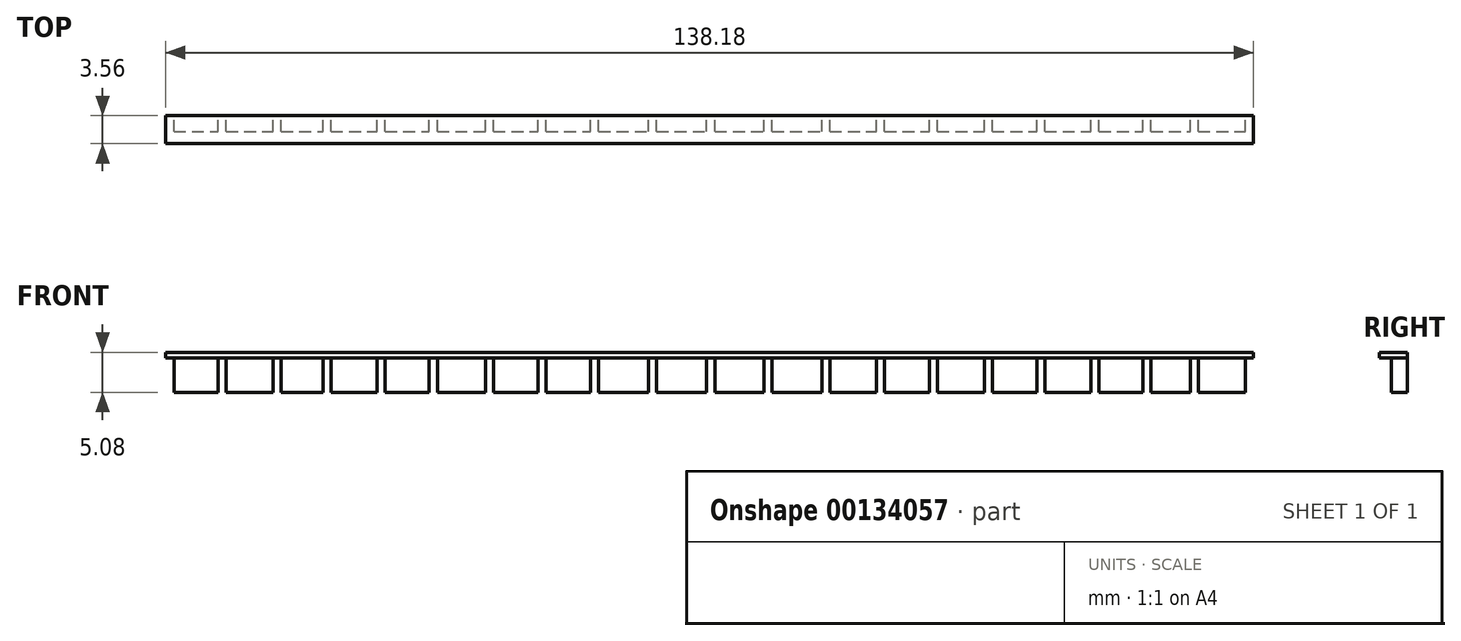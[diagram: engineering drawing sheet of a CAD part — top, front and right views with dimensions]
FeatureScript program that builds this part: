
annotation { "Feature Type Name" : "Feature", "Feature Type Description" : "" }
export const myFeature = defineFeature(function(context is Context, id is Id, definition is map)
    precondition{}
    {
        {
            var Q0;
            Q0=qCreatedBy(makeId("Front.planeOp"),FACE);
            var sketch = newSketch(context, id + "F0", { "sketchPlane" : qUnion([Q0])});
            skLineSegment(sketch, "E0.bottom", {"start": v(69.09, 2.54) * mm, "end": v(-69.09, 2.54) * mm});
            skLineSegment(sketch, "E0.top", {"start": v(69.09, -2.54) * mm, "end": v(-69.09, -2.54) * mm});
            skLineSegment(sketch, "E0.left", {"start": v(69.09, 2.54) * mm, "end": v(69.09, -2.54) * mm});
            skLineSegment(sketch, "E0.right", {"start": v(-69.09, 2.54) * mm, "end": v(-69.09, -2.54) * mm});
            skPoint(sketch, "E0.middle", {"position": v(0, 0) * mm});
            skLineSegment(sketch, "E1", {"start": v(-69.09, 1.8) * mm, "end": v(69.09, 1.8) * mm});
            skLineSegment(sketch, "E2.bottom", {"start": v(69.09, -2.54) * mm, "end": v(68.05, -2.54) * mm});
            skLineSegment(sketch, "E2.top", {"start": v(69.09, 1.8) * mm, "end": v(68.05, 1.8) * mm});
            skLineSegment(sketch, "E2.left", {"start": v(69.09, -2.54) * mm, "end": v(69.09, 1.8) * mm});
            skLineSegment(sketch, "E2.right", {"start": v(68.05, -2.54) * mm, "end": v(68.05, 1.8) * mm});
            skLineSegment(sketch, "E3.bottom", {"start": v(62.09, -2.54) * mm, "end": v(61.12, -2.54) * mm});
            skLineSegment(sketch, "E3.top", {"start": v(62.09, 1.8) * mm, "end": v(61.12, 1.8) * mm});
            skLineSegment(sketch, "E3.left", {"start": v(62.09, -2.54) * mm, "end": v(62.09, 1.8) * mm});
            skLineSegment(sketch, "E3.right", {"start": v(61.12, -2.54) * mm, "end": v(61.12, 1.8) * mm});
            skLineSegment(sketch, "E4.bottom", {"start": v(56.07, -2.54) * mm, "end": v(55.05, -2.54) * mm});
            skLineSegment(sketch, "E4.top", {"start": v(56.07, 1.8) * mm, "end": v(55.05, 1.8) * mm});
            skLineSegment(sketch, "E4.left", {"start": v(56.07, -2.54) * mm, "end": v(56.07, 1.8) * mm});
            skLineSegment(sketch, "E4.right", {"start": v(55.05, -2.54) * mm, "end": v(55.05, 1.8) * mm});
            skLineSegment(sketch, "E5.bottom", {"start": v(49.46, -2.54) * mm, "end": v(48.44, -2.54) * mm});
            skLineSegment(sketch, "E5.top", {"start": v(49.46, 1.8) * mm, "end": v(48.44, 1.8) * mm});
            skLineSegment(sketch, "E5.left", {"start": v(49.46, -2.54) * mm, "end": v(49.46, 1.8) * mm});
            skLineSegment(sketch, "E5.right", {"start": v(48.44, -2.54) * mm, "end": v(48.44, 1.8) * mm});
            skLineSegment(sketch, "E6.bottom", {"start": v(42.59, -2.54) * mm, "end": v(41.57, -2.54) * mm});
            skLineSegment(sketch, "E6.top", {"start": v(42.59, 1.8) * mm, "end": v(41.57, 1.8) * mm});
            skLineSegment(sketch, "E6.left", {"start": v(42.59, -2.54) * mm, "end": v(42.59, 1.8) * mm});
            skLineSegment(sketch, "E6.right", {"start": v(41.57, -2.54) * mm, "end": v(41.57, 1.8) * mm});
            skLineSegment(sketch, "E7.bottom", {"start": v(35.92, -2.54) * mm, "end": v(34.9, -2.54) * mm});
            skLineSegment(sketch, "E7.top", {"start": v(35.92, 1.8) * mm, "end": v(34.9, 1.8) * mm});
            skLineSegment(sketch, "E7.left", {"start": v(35.92, -2.54) * mm, "end": v(35.92, 1.8) * mm});
            skLineSegment(sketch, "E7.right", {"start": v(34.9, -2.54) * mm, "end": v(34.9, 1.8) * mm});
            skLineSegment(sketch, "E8.bottom", {"start": v(28.94, -2.54) * mm, "end": v(27.92, -2.54) * mm});
            skLineSegment(sketch, "E8.top", {"start": v(28.94, 1.8) * mm, "end": v(27.92, 1.8) * mm});
            skLineSegment(sketch, "E8.left", {"start": v(28.94, -2.54) * mm, "end": v(28.94, 1.8) * mm});
            skLineSegment(sketch, "E8.right", {"start": v(27.92, -2.54) * mm, "end": v(27.92, 1.8) * mm});
            skLineSegment(sketch, "E9.bottom", {"start": v(22.23, -2.54) * mm, "end": v(21.2, -2.54) * mm});
            skLineSegment(sketch, "E9.top", {"start": v(22.23, 1.8) * mm, "end": v(21.2, 1.8) * mm});
            skLineSegment(sketch, "E9.left", {"start": v(22.23, -2.54) * mm, "end": v(22.23, 1.8) * mm});
            skLineSegment(sketch, "E9.right", {"start": v(21.2, -2.54) * mm, "end": v(21.2, 1.8) * mm});
            skLineSegment(sketch, "E10.bottom", {"start": v(15.3, -2.54) * mm, "end": v(14.27, -2.54) * mm});
            skLineSegment(sketch, "E10.top", {"start": v(15.3, 1.8) * mm, "end": v(14.27, 1.8) * mm});
            skLineSegment(sketch, "E10.left", {"start": v(15.3, -2.54) * mm, "end": v(15.3, 1.8) * mm});
            skLineSegment(sketch, "E10.right", {"start": v(14.27, -2.54) * mm, "end": v(14.27, 1.8) * mm});
            skLineSegment(sketch, "E11.bottom", {"start": v(7.94, -2.54) * mm, "end": v(6.91, -2.54) * mm});
            skLineSegment(sketch, "E11.top", {"start": v(7.94, 1.8) * mm, "end": v(6.91, 1.8) * mm});
            skLineSegment(sketch, "E11.left", {"start": v(7.94, -2.54) * mm, "end": v(7.94, 1.8) * mm});
            skLineSegment(sketch, "E11.right", {"start": v(6.91, -2.54) * mm, "end": v(6.91, 1.8) * mm});
            skLineSegment(sketch, "E12.bottom", {"start": v(0.68, -2.54) * mm, "end": v(-0.37, -2.54) * mm});
            skLineSegment(sketch, "E12.top", {"start": v(0.68, 1.8) * mm, "end": v(-0.37, 1.8) * mm});
            skLineSegment(sketch, "E12.left", {"start": v(0.68, -2.54) * mm, "end": v(0.68, 1.8) * mm});
            skLineSegment(sketch, "E12.right", {"start": v(-0.37, -2.54) * mm, "end": v(-0.37, 1.8) * mm});
            skLineSegment(sketch, "E13.bottom", {"start": v(-6.72, -2.54) * mm, "end": v(-7.73, -2.54) * mm});
            skLineSegment(sketch, "E13.top", {"start": v(-6.72, 1.8) * mm, "end": v(-7.73, 1.8) * mm});
            skLineSegment(sketch, "E13.left", {"start": v(-6.72, -2.54) * mm, "end": v(-6.72, 1.8) * mm});
            skLineSegment(sketch, "E13.right", {"start": v(-7.73, -2.54) * mm, "end": v(-7.73, 1.8) * mm});
            skLineSegment(sketch, "E14.bottom", {"start": v(-14.09, -2.54) * mm, "end": v(-15.13, -2.54) * mm});
            skLineSegment(sketch, "E14.top", {"start": v(-14.09, 1.8) * mm, "end": v(-15.13, 1.8) * mm});
            skLineSegment(sketch, "E14.left", {"start": v(-14.09, -2.54) * mm, "end": v(-14.09, 1.8) * mm});
            skLineSegment(sketch, "E14.right", {"start": v(-15.13, -2.54) * mm, "end": v(-15.13, 1.8) * mm});
            skLineSegment(sketch, "E15.bottom", {"start": v(-20.76, -2.54) * mm, "end": v(-21.8, -2.54) * mm});
            skLineSegment(sketch, "E15.top", {"start": v(-20.76, 1.8) * mm, "end": v(-21.8, 1.8) * mm});
            skLineSegment(sketch, "E15.left", {"start": v(-20.76, -2.54) * mm, "end": v(-20.76, 1.8) * mm});
            skLineSegment(sketch, "E15.right", {"start": v(-21.8, -2.54) * mm, "end": v(-21.8, 1.8) * mm});
            skLineSegment(sketch, "E16.bottom", {"start": v(-27.44, -2.54) * mm, "end": v(-28.46, -2.54) * mm});
            skLineSegment(sketch, "E16.top", {"start": v(-27.44, 1.8) * mm, "end": v(-28.46, 1.8) * mm});
            skLineSegment(sketch, "E16.left", {"start": v(-27.44, -2.54) * mm, "end": v(-27.44, 1.8) * mm});
            skLineSegment(sketch, "E16.right", {"start": v(-28.46, -2.54) * mm, "end": v(-28.46, 1.8) * mm});
            skLineSegment(sketch, "E17.bottom", {"start": v(-34.57, -2.54) * mm, "end": v(-35.6, -2.54) * mm});
            skLineSegment(sketch, "E17.top", {"start": v(-34.57, 1.8) * mm, "end": v(-35.6, 1.8) * mm});
            skLineSegment(sketch, "E17.left", {"start": v(-34.57, -2.54) * mm, "end": v(-34.57, 1.8) * mm});
            skLineSegment(sketch, "E17.right", {"start": v(-35.6, -2.54) * mm, "end": v(-35.6, 1.8) * mm});
            skLineSegment(sketch, "E18.bottom", {"start": v(-41.2, -2.54) * mm, "end": v(-42.23, -2.54) * mm});
            skLineSegment(sketch, "E18.top", {"start": v(-41.2, 1.8) * mm, "end": v(-42.23, 1.8) * mm});
            skLineSegment(sketch, "E18.left", {"start": v(-41.2, -2.54) * mm, "end": v(-41.2, 1.8) * mm});
            skLineSegment(sketch, "E18.right", {"start": v(-42.23, -2.54) * mm, "end": v(-42.23, 1.8) * mm});
            skLineSegment(sketch, "E19.bottom", {"start": v(-48.08, -2.54) * mm, "end": v(-49.1, -2.54) * mm});
            skLineSegment(sketch, "E19.top", {"start": v(-48.08, 1.8) * mm, "end": v(-49.1, 1.8) * mm});
            skLineSegment(sketch, "E19.left", {"start": v(-48.08, -2.54) * mm, "end": v(-48.08, 1.8) * mm});
            skLineSegment(sketch, "E19.right", {"start": v(-49.1, -2.54) * mm, "end": v(-49.1, 1.8) * mm});
            skLineSegment(sketch, "E20.bottom", {"start": v(-54.41, -2.54) * mm, "end": v(-55.44, -2.54) * mm});
            skLineSegment(sketch, "E20.top", {"start": v(-54.41, 1.8) * mm, "end": v(-55.44, 1.8) * mm});
            skLineSegment(sketch, "E20.left", {"start": v(-54.41, -2.54) * mm, "end": v(-54.41, 1.8) * mm});
            skLineSegment(sketch, "E20.right", {"start": v(-55.44, -2.54) * mm, "end": v(-55.44, 1.8) * mm});
            skLineSegment(sketch, "E21.bottom", {"start": v(-61.4, -2.54) * mm, "end": v(-62.43, -2.54) * mm});
            skLineSegment(sketch, "E21.top", {"start": v(-61.4, 1.8) * mm, "end": v(-62.43, 1.8) * mm});
            skLineSegment(sketch, "E21.left", {"start": v(-61.4, -2.54) * mm, "end": v(-61.4, 1.8) * mm});
            skLineSegment(sketch, "E21.right", {"start": v(-62.43, -2.54) * mm, "end": v(-62.43, 1.8) * mm});
            skLineSegment(sketch, "E22.bottom", {"start": v(-69.09, -2.54) * mm, "end": v(-68.04, -2.54) * mm});
            skLineSegment(sketch, "E22.top", {"start": v(-69.09, 1.8) * mm, "end": v(-68.04, 1.8) * mm});
            skLineSegment(sketch, "E22.left", {"start": v(-69.09, -2.54) * mm, "end": v(-69.09, 1.8) * mm});
            skLineSegment(sketch, "E22.right", {"start": v(-68.04, -2.54) * mm, "end": v(-68.04, 1.8) * mm});
            skSolve(sketch);
        }
        {
            var Q0;
            Q0=makeQuery(id+"F0.imprint","IMPRINT",FACE,{"disambiguationData":[TD([[makeQuery(id+"F0.imprint","IMPRINT",EDGE,{"derivedFrom":sQuery(id+"F0.wireOp",EDGE,"E22.bottom")}),1.0]])]});
            var Q1;
            Q1=makeQuery(id+"F0.imprint","IMPRINT",FACE,{"disambiguationData":[TD([[makeQuery(id+"F0.imprint","IMPRINT",EDGE,{"derivedFrom":sQuery(id+"F0.wireOp",EDGE,"E0.bottom")}),1.0]])]});
            var Q2;
            Q2=makeQuery(id+"F0.imprint","IMPRINT",FACE,{"disambiguationData":[TD([[makeQuery(id+"F0.imprint","IMPRINT",EDGE,{"derivedFrom":sQuery(id+"F0.wireOp",EDGE,"E21.bottom")}),-1.0]])]});
            var Q3;
            Q3=makeQuery(id+"F0.imprint","IMPRINT",FACE,{"disambiguationData":[TD([[makeQuery(id+"F0.imprint","IMPRINT",EDGE,{"derivedFrom":sQuery(id+"F0.wireOp",EDGE,"E20.bottom")}),-1.0]])]});
            var Q4;
            Q4=makeQuery(id+"F0.imprint","IMPRINT",FACE,{"disambiguationData":[TD([[makeQuery(id+"F0.imprint","IMPRINT",EDGE,{"derivedFrom":sQuery(id+"F0.wireOp",EDGE,"E19.bottom")}),-1.0]])]});
            var Q5;
            Q5=makeQuery(id+"F0.imprint","IMPRINT",FACE,{"disambiguationData":[TD([[makeQuery(id+"F0.imprint","IMPRINT",EDGE,{"derivedFrom":sQuery(id+"F0.wireOp",EDGE,"E18.bottom")}),-1.0]])]});
            var Q6;
            Q6=makeQuery(id+"F0.imprint","IMPRINT",FACE,{"disambiguationData":[TD([[makeQuery(id+"F0.imprint","IMPRINT",EDGE,{"derivedFrom":sQuery(id+"F0.wireOp",EDGE,"E17.bottom")}),-1.0]])]});
            var Q7;
            Q7=makeQuery(id+"F0.imprint","IMPRINT",FACE,{"disambiguationData":[TD([[makeQuery(id+"F0.imprint","IMPRINT",EDGE,{"derivedFrom":sQuery(id+"F0.wireOp",EDGE,"E16.bottom")}),-1.0]])]});
            var Q8;
            Q8=makeQuery(id+"F0.imprint","IMPRINT",FACE,{"disambiguationData":[TD([[makeQuery(id+"F0.imprint","IMPRINT",EDGE,{"derivedFrom":sQuery(id+"F0.wireOp",EDGE,"E15.bottom")}),-1.0]])]});
            var Q9;
            Q9=makeQuery(id+"F0.imprint","IMPRINT",FACE,{"disambiguationData":[TD([[makeQuery(id+"F0.imprint","IMPRINT",EDGE,{"derivedFrom":sQuery(id+"F0.wireOp",EDGE,"E14.bottom")}),-1.0]])]});
            var Q10;
            Q10=makeQuery(id+"F0.imprint","IMPRINT",FACE,{"disambiguationData":[TD([[makeQuery(id+"F0.imprint","IMPRINT",EDGE,{"derivedFrom":sQuery(id+"F0.wireOp",EDGE,"E13.bottom")}),-1.0]])]});
            var Q11;
            Q11=makeQuery(id+"F0.imprint","IMPRINT",FACE,{"disambiguationData":[TD([[makeQuery(id+"F0.imprint","IMPRINT",EDGE,{"derivedFrom":sQuery(id+"F0.wireOp",EDGE,"E12.bottom")}),-1.0]])]});
            var Q12;
            Q12=makeQuery(id+"F0.imprint","IMPRINT",FACE,{"disambiguationData":[TD([[makeQuery(id+"F0.imprint","IMPRINT",EDGE,{"derivedFrom":sQuery(id+"F0.wireOp",EDGE,"E11.bottom")}),-1.0]])]});
            var Q13;
            Q13=makeQuery(id+"F0.imprint","IMPRINT",FACE,{"disambiguationData":[TD([[makeQuery(id+"F0.imprint","IMPRINT",EDGE,{"derivedFrom":sQuery(id+"F0.wireOp",EDGE,"E10.bottom")}),-1.0]])]});
            var Q14;
            Q14=makeQuery(id+"F0.imprint","IMPRINT",FACE,{"disambiguationData":[TD([[makeQuery(id+"F0.imprint","IMPRINT",EDGE,{"derivedFrom":sQuery(id+"F0.wireOp",EDGE,"E9.bottom")}),-1.0]])]});
            var Q15;
            Q15=makeQuery(id+"F0.imprint","IMPRINT",FACE,{"disambiguationData":[TD([[makeQuery(id+"F0.imprint","IMPRINT",EDGE,{"derivedFrom":sQuery(id+"F0.wireOp",EDGE,"E8.bottom")}),-1.0]])]});
            var Q16;
            Q16=makeQuery(id+"F0.imprint","IMPRINT",FACE,{"disambiguationData":[TD([[makeQuery(id+"F0.imprint","IMPRINT",EDGE,{"derivedFrom":sQuery(id+"F0.wireOp",EDGE,"E7.bottom")}),-1.0]])]});
            var Q17;
            Q17=makeQuery(id+"F0.imprint","IMPRINT",FACE,{"disambiguationData":[TD([[makeQuery(id+"F0.imprint","IMPRINT",EDGE,{"derivedFrom":sQuery(id+"F0.wireOp",EDGE,"E6.bottom")}),-1.0]])]});
            var Q18;
            Q18=makeQuery(id+"F0.imprint","IMPRINT",FACE,{"disambiguationData":[TD([[makeQuery(id+"F0.imprint","IMPRINT",EDGE,{"derivedFrom":sQuery(id+"F0.wireOp",EDGE,"E5.bottom")}),-1.0]])]});
            var Q19;
            Q19=makeQuery(id+"F0.imprint","IMPRINT",FACE,{"disambiguationData":[TD([[makeQuery(id+"F0.imprint","IMPRINT",EDGE,{"derivedFrom":sQuery(id+"F0.wireOp",EDGE,"E4.bottom")}),-1.0]])]});
            var Q20;
            Q20=makeQuery(id+"F0.imprint","IMPRINT",FACE,{"disambiguationData":[TD([[makeQuery(id+"F0.imprint","IMPRINT",EDGE,{"derivedFrom":sQuery(id+"F0.wireOp",EDGE,"E3.bottom")}),-1.0]])]});
            var Q21;
            Q21=makeQuery(id+"F0.imprint","IMPRINT",FACE,{"disambiguationData":[TD([[makeQuery(id+"F0.imprint","IMPRINT",EDGE,{"derivedFrom":sQuery(id+"F0.wireOp",EDGE,"E2.bottom")}),-1.0]])]});
            extrude(context, id + "F1", {"entities" : qUnion([Q0, Q1, Q2, Q3, Q4, Q5, Q6, Q7, Q8, Q9, Q10, Q11, Q12, Q13, Q14, Q15, Q16, Q17, Q18, Q19, Q20, Q21]), "depth" : 3.56 * mm});
        }
        {
            var Q0;
            {var subQ2=sQuery(id+"F0.wireOp",EDGE,"E21.right");Q0=makeQuery(id+"F0.imprint","IMPRINT",FACE,{"disambiguationData":[TD([[makeQuery(id+"F0.imprint","IMPRINT",EDGE,{"derivedFrom":subQ2}),1.0]])]});}
            var Q1;
            {var subQ0=sQuery(id+"F0.wireOp",EDGE,"E20.right");Q1=makeQuery(id+"F0.imprint","IMPRINT",FACE,{"disambiguationData":[TD([[makeQuery(id+"F0.imprint","IMPRINT",EDGE,{"derivedFrom":subQ0}),1.0]])]});}
            var Q2;
            {var subQ0=sQuery(id+"F0.wireOp",EDGE,"E19.right");Q2=makeQuery(id+"F0.imprint","IMPRINT",FACE,{"disambiguationData":[TD([[makeQuery(id+"F0.imprint","IMPRINT",EDGE,{"derivedFrom":subQ0}),1.0]])]});}
            var Q3;
            {var subQ0=sQuery(id+"F0.wireOp",EDGE,"E18.right");Q3=makeQuery(id+"F0.imprint","IMPRINT",FACE,{"disambiguationData":[TD([[makeQuery(id+"F0.imprint","IMPRINT",EDGE,{"derivedFrom":subQ0}),1.0]])]});}
            var Q4;
            {var subQ0=sQuery(id+"F0.wireOp",EDGE,"E17.right");Q4=makeQuery(id+"F0.imprint","IMPRINT",FACE,{"disambiguationData":[TD([[makeQuery(id+"F0.imprint","IMPRINT",EDGE,{"derivedFrom":subQ0}),1.0]])]});}
            var Q5;
            {var subQ0=sQuery(id+"F0.wireOp",EDGE,"E16.right");Q5=makeQuery(id+"F0.imprint","IMPRINT",FACE,{"disambiguationData":[TD([[makeQuery(id+"F0.imprint","IMPRINT",EDGE,{"derivedFrom":subQ0}),1.0]])]});}
            var Q6;
            {var subQ0=sQuery(id+"F0.wireOp",EDGE,"E15.right");Q6=makeQuery(id+"F0.imprint","IMPRINT",FACE,{"disambiguationData":[TD([[makeQuery(id+"F0.imprint","IMPRINT",EDGE,{"derivedFrom":subQ0}),1.0]])]});}
            var Q7;
            {var subQ0=sQuery(id+"F0.wireOp",EDGE,"E14.right");Q7=makeQuery(id+"F0.imprint","IMPRINT",FACE,{"disambiguationData":[TD([[makeQuery(id+"F0.imprint","IMPRINT",EDGE,{"derivedFrom":subQ0}),1.0]])]});}
            var Q8;
            {var subQ0=sQuery(id+"F0.wireOp",EDGE,"E13.right");Q8=makeQuery(id+"F0.imprint","IMPRINT",FACE,{"disambiguationData":[TD([[makeQuery(id+"F0.imprint","IMPRINT",EDGE,{"derivedFrom":subQ0}),1.0]])]});}
            var Q9;
            {var subQ0=sQuery(id+"F0.wireOp",EDGE,"E12.right");Q9=makeQuery(id+"F0.imprint","IMPRINT",FACE,{"disambiguationData":[TD([[makeQuery(id+"F0.imprint","IMPRINT",EDGE,{"derivedFrom":subQ0}),1.0]])]});}
            var Q10;
            {var subQ0=sQuery(id+"F0.wireOp",EDGE,"E11.right");Q10=makeQuery(id+"F0.imprint","IMPRINT",FACE,{"disambiguationData":[TD([[makeQuery(id+"F0.imprint","IMPRINT",EDGE,{"derivedFrom":subQ0}),1.0]])]});}
            var Q11;
            {var subQ0=sQuery(id+"F0.wireOp",EDGE,"E10.right");Q11=makeQuery(id+"F0.imprint","IMPRINT",FACE,{"disambiguationData":[TD([[makeQuery(id+"F0.imprint","IMPRINT",EDGE,{"derivedFrom":subQ0}),1.0]])]});}
            var Q12;
            {var subQ0=sQuery(id+"F0.wireOp",EDGE,"E9.right");Q12=makeQuery(id+"F0.imprint","IMPRINT",FACE,{"disambiguationData":[TD([[makeQuery(id+"F0.imprint","IMPRINT",EDGE,{"derivedFrom":subQ0}),1.0]])]});}
            var Q13;
            {var subQ0=sQuery(id+"F0.wireOp",EDGE,"E8.right");Q13=makeQuery(id+"F0.imprint","IMPRINT",FACE,{"disambiguationData":[TD([[makeQuery(id+"F0.imprint","IMPRINT",EDGE,{"derivedFrom":subQ0}),1.0]])]});}
            var Q14;
            {var subQ0=sQuery(id+"F0.wireOp",EDGE,"E7.right");Q14=makeQuery(id+"F0.imprint","IMPRINT",FACE,{"disambiguationData":[TD([[makeQuery(id+"F0.imprint","IMPRINT",EDGE,{"derivedFrom":subQ0}),1.0]])]});}
            var Q15;
            {var subQ0=sQuery(id+"F0.wireOp",EDGE,"E6.right");Q15=makeQuery(id+"F0.imprint","IMPRINT",FACE,{"disambiguationData":[TD([[makeQuery(id+"F0.imprint","IMPRINT",EDGE,{"derivedFrom":subQ0}),1.0]])]});}
            var Q16;
            {var subQ0=sQuery(id+"F0.wireOp",EDGE,"E5.right");Q16=makeQuery(id+"F0.imprint","IMPRINT",FACE,{"disambiguationData":[TD([[makeQuery(id+"F0.imprint","IMPRINT",EDGE,{"derivedFrom":subQ0}),1.0]])]});}
            var Q17;
            {var subQ0=sQuery(id+"F0.wireOp",EDGE,"E4.right");Q17=makeQuery(id+"F0.imprint","IMPRINT",FACE,{"disambiguationData":[TD([[makeQuery(id+"F0.imprint","IMPRINT",EDGE,{"derivedFrom":subQ0}),1.0]])]});}
            var Q18;
            {var subQ0=sQuery(id+"F0.wireOp",EDGE,"E3.right");Q18=makeQuery(id+"F0.imprint","IMPRINT",FACE,{"disambiguationData":[TD([[makeQuery(id+"F0.imprint","IMPRINT",EDGE,{"derivedFrom":subQ0}),1.0]])]});}
            var Q19;
            {var subQ0=sQuery(id+"F0.wireOp",EDGE,"E2.right");Q19=makeQuery(id+"F0.imprint","IMPRINT",FACE,{"disambiguationData":[TD([[makeQuery(id+"F0.imprint","IMPRINT",EDGE,{"derivedFrom":subQ0}),1.0]])]});}
            extrude(context, id + "F2", {"entities" : qUnion([Q0, Q1, Q2, Q3, Q4, Q5, Q6, Q7, Q8, Q9, Q10, Q11, Q12, Q13, Q14, Q15, Q16, Q17, Q18, Q19]), "operationType" : NewBodyOperationType.ADD, "depth" : 2.03 * mm});
        }
    });
